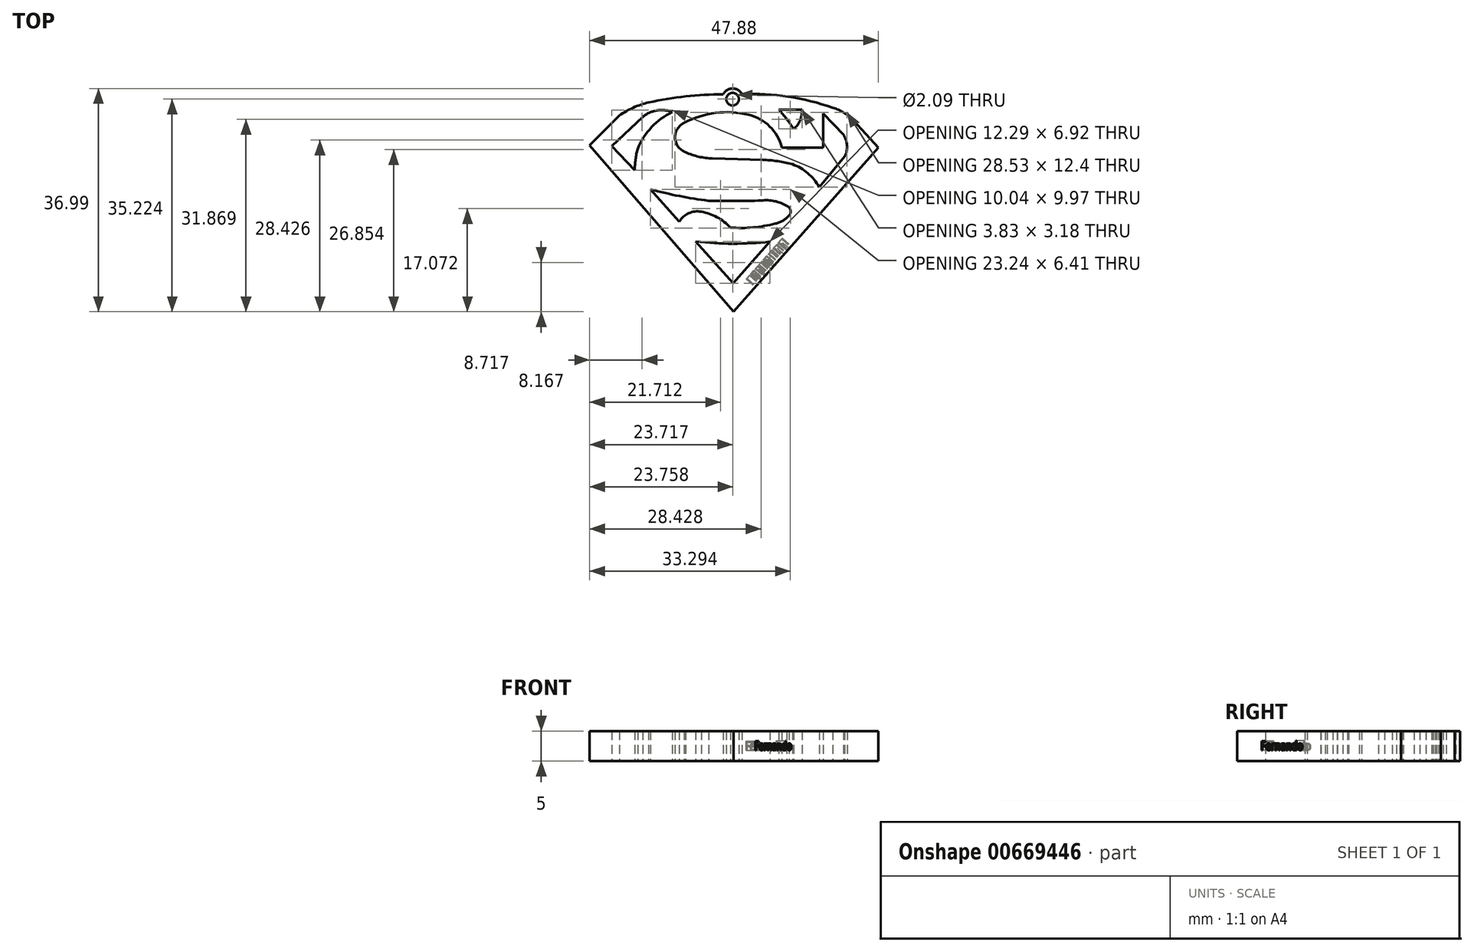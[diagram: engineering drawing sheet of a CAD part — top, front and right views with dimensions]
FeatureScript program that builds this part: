
annotation { "Feature Type Name" : "Feature", "Feature Type Description" : "" }
export const myFeature = defineFeature(function(context is Context, id is Id, definition is map)
    precondition{}
    {
        {
            var Q0;
            Q0=qCreatedBy(makeId("Top.planeOp"),FACE);
            var sketch = newSketch(context, id + "F0", { "sketchPlane" : qUnion([Q0])});
            skLineSegment(sketch, "E0", {"start": v(100, 0) * mm, "end": v(-100, 0) * mm, "construction": true});
            skLineSegment(sketch, "E1", {"start": v(0, 100) * mm, "end": v(0, -100) * mm, "construction": true});
            skLineSegment(sketch, "E2", {"start": v(18.8, 12.4) * mm, "end": v(24.97, 5.49) * mm});
            skLineSegment(sketch, "E3", {"start": v(24.97, 5.49) * mm, "end": v(31.09, 12.38) * mm});
            skArc(sketch, "E4", {"start": v(18.8, 12.4) * mm, "mid": v(24.94, 12.04) * mm, "end": v(31.09, 12.38) * mm});
            skLineSegment(sketch, "E5", {"start": v(11.27, 21.06) * mm, "end": v(16.05, 15.68) * mm});
            skArc(sketch, "E6", {"start": v(24.51, 14.72) * mm, "mid": v(22.32, 16.44) * mm, "end": v(19.7, 17.34) * mm});
            skArc(sketch, "E7", {"start": v(24.51, 14.72) * mm, "mid": v(28.27, 14.74) * mm, "end": v(31.98, 15.39) * mm});
            skArc(sketch, "E8", {"start": v(31.98, 15.39) * mm, "mid": v(33.22, 15.86) * mm, "end": v(34.25, 16.7) * mm});
            skArc(sketch, "E9", {"start": v(19.7, 17.34) * mm, "mid": v(17.61, 17.09) * mm, "end": v(16.05, 15.68) * mm});
            skArc(sketch, "E10", {"start": v(34.25, 16.7) * mm, "mid": v(34.48, 17.61) * mm, "end": v(33.85, 18.32) * mm});
            skArc(sketch, "E11", {"start": v(33.85, 18.32) * mm, "mid": v(31.83, 19.1) * mm, "end": v(29.66, 19.19) * mm});
            skArc(sketch, "E12", {"start": v(11.27, 21.06) * mm, "mid": v(16.07, 19.94) * mm, "end": v(20.93, 19.16) * mm});
            skArc(sketch, "E13", {"start": v(20.93, 19.16) * mm, "mid": v(25.3, 19.11) * mm, "end": v(29.66, 19.19) * mm});
            skLineSegment(sketch, "E14", {"start": v(39.91, 33.65) * mm, "end": v(39.91, 27.97) * mm});
            skLineSegment(sketch, "E15", {"start": v(39.91, 27.97) * mm, "end": v(33.05, 27.97) * mm});
            skArc(sketch, "E16", {"start": v(33.05, 27.97) * mm, "mid": v(31.04, 31.48) * mm, "end": v(27.5, 33.43) * mm});
            skArc(sketch, "E17", {"start": v(27.5, 33.43) * mm, "mid": v(22.06, 33.72) * mm, "end": v(16.87, 32.07) * mm});
            skArc(sketch, "E18", {"start": v(16.87, 32.07) * mm, "mid": v(15.35, 29.56) * mm, "end": v(17.11, 27.2) * mm});
            skArc(sketch, "E19", {"start": v(17.11, 27.2) * mm, "mid": v(19.27, 26.47) * mm, "end": v(21.53, 26.17) * mm});
            skLineSegment(sketch, "E20", {"start": v(21.53, 26.17) * mm, "end": v(29.84, 25.94) * mm});
            skArc(sketch, "E21", {"start": v(34.8, 25.2) * mm, "mid": v(32.35, 25.72) * mm, "end": v(29.84, 25.94) * mm});
            skArc(sketch, "E22", {"start": v(39.25, 21.43) * mm, "mid": v(37.37, 23.73) * mm, "end": v(34.8, 25.2) * mm});
            skLineSegment(sketch, "E23", {"start": v(39.25, 21.43) * mm, "end": v(43.49, 26.5) * mm});
            skArc(sketch, "E24", {"start": v(43.49, 26.5) * mm, "mid": v(43.87, 28.34) * mm, "end": v(43.24, 30.12) * mm});
            skLineSegment(sketch, "E25", {"start": v(43.24, 30.12) * mm, "end": v(39.91, 33.65) * mm});
            skLineSegment(sketch, "E26", {"start": v(32.56, 34.24) * mm, "end": v(36.38, 34.24) * mm});
            skArc(sketch, "E27", {"start": v(35.03, 31.06) * mm, "mid": v(36.09, 32.48) * mm, "end": v(36.38, 34.24) * mm});
            skArc(sketch, "E28", {"start": v(35.03, 31.06) * mm, "mid": v(33.86, 32.7) * mm, "end": v(32.56, 34.24) * mm});
            skLineSegment(sketch, "E29", {"start": v(4.88, 28.24) * mm, "end": v(8.65, 24.22) * mm});
            skArc(sketch, "E30", {"start": v(9.14, 27.8) * mm, "mid": v(8.8, 26.03) * mm, "end": v(8.65, 24.22) * mm});
            skArc(sketch, "E31", {"start": v(14.92, 33.87) * mm, "mid": v(11.47, 31.37) * mm, "end": v(9.14, 27.8) * mm});
            skArc(sketch, "E32", {"start": v(14.92, 33.87) * mm, "mid": v(13.6, 34.17) * mm, "end": v(12.25, 34.12) * mm});
            skArc(sketch, "E33", {"start": v(12.25, 34.12) * mm, "mid": v(11.06, 33.73) * mm, "end": v(10, 33.06) * mm});
            skLineSegment(sketch, "E34", {"start": v(4.88, 28.24) * mm, "end": v(10, 33.06) * mm});
            skLineSegment(sketch, "E35", {"start": v(25.06, 0.78) * mm, "end": v(49.06, 27.95) * mm});
            skLineSegment(sketch, "E36", {"start": v(25.06, 0.78) * mm, "end": v(1.18, 28.36) * mm});
            skLineSegment(sketch, "E37", {"start": v(1.18, 28.36) * mm, "end": v(6.1, 33.29) * mm});
            skLineSegment(sketch, "E38", {"start": v(49.06, 27.95) * mm, "end": v(44.9, 32.46) * mm});
            skArc(sketch, "E39", {"start": v(10.98, 35.46) * mm, "mid": v(8.44, 34.6) * mm, "end": v(6.1, 33.29) * mm});
            skArc(sketch, "E40", {"start": v(44.9, 32.46) * mm, "mid": v(43.34, 33.75) * mm, "end": v(41.5, 34.58) * mm});
            skArc(sketch, "E41", {"start": v(41.5, 34.58) * mm, "mid": v(34.1, 36.41) * mm, "end": v(26.47, 36.8) * mm});
            skArc(sketch, "E42", {"start": v(26.47, 36.8) * mm, "mid": v(24.9, 37.77) * mm, "end": v(23.32, 36.8) * mm});
            skCircle(sketch, "E43", {"center": v(24.9, 36) * mm, "radius": 1.04 * mm});
            skArc(sketch, "E44.trimOffspring", {"start": v(23.32, 36.8) * mm, "mid": v(17.11, 36.44) * mm, "end": v(10.98, 35.46) * mm});
            skPoint(sketch, "E45.start.orphan", {"position": v(25.7, 36.75) * mm});
            skSolve(sketch);
        }
        {
            var Q0;
            Q0 = qSketchRegion(id + "F0", true);
            extrude(context, id + "F1", {"entities" : qUnion([Q0]), "depth" : 5 * mm, "offsetDistance" : 25 * mm});
        }
        {
            var Q0;
            Q0=makeQuery(id+"F1.opExtrude","SWEPT_FACE",FACE,{"disambiguationData":[OSD([sQuery(id+"F0.wireOp",EDGE,"E35")])]});
            var sketch = newSketch(context, id + "F2", { "sketchPlane" : qUnion([Q0])});
            skText(sketch, "E46", { "text": "Fernando\n", "fontName": "OpenSans-Regular.ttf"});
            const initialGuessF2  = {"E46": [0.02242, 0.00183, 1, 0, 0.0015]};
            skSetInitialGuess(sketch, initialGuessF2);
            skSolve(sketch);
        }
        {
            var Q0;
            Q0 = qSketchRegion(id + "F2", true);
            extrude(context, id + "F3", {"entities" : qUnion([Q0]), "operationType" : NewBodyOperationType.REMOVE, "oppositeDirection" : true, "depth" : 2 * mm, "offsetDistance" : 25 * mm});
        }
    });
